# Revit family: AFX-Pearl_Pendant-1
name_source: partatom
category: Lighting Fixtures
units: mm (PartAtom-declared; Revit-internal decimal feet)

## family parameters
Cut with Voids When Loaded = No
Host = Face
Light Source = Yes
Part Type = Normal
Room Calculation Point = No
Round Connector Dimension = Use Diameter
Shared = No

## types (1)
- PRLP24L30D1BK
    Apparent Load = 0 VA
    Assembly Code = D5020200
    Color Filter = 16777215
    Colour Rendering Index = 90
    Connector Rigid Shank Finish = AFX - Black Steel
    Cover Finish = AFX - Black Steel
    Default Elevation = 48"
    Description = Simplistic small globe LED pendant with three adjustable arms - 24"Diameter x 17"H
    Diameter = 24"
    Diffuser Finish = AFX - White Acrylic
    Dimming Lamp Color Temperature Shift = <None>
    Frame Finish = AFX - Black Steel
    Height = 17"
    Housing Finish = AFX - Black Steel
    Keynote = 12500
    LED Finish = AFX - White Plastic
    Manufacturer = AFX Inc
    Model = PRLP24L30D1BK
    Photometric Web File = PRLP24L30D1xx_IES.IES
    Product Documentation Link = https://www.afxinc.com
    Revit File Built By = https://servex-us.com
    Rigid Shank Finish = AFX - Black Steel
    Tilt Angle = 0.00°
    Type Comments = Pearl
    URL = https://www.afxinc.com
    Voltage = 120 V
    Wattage Comments = 40

## geometry (parser evidence)
native form markers: Sweep x25
no freeform markers — native parametric forms only
